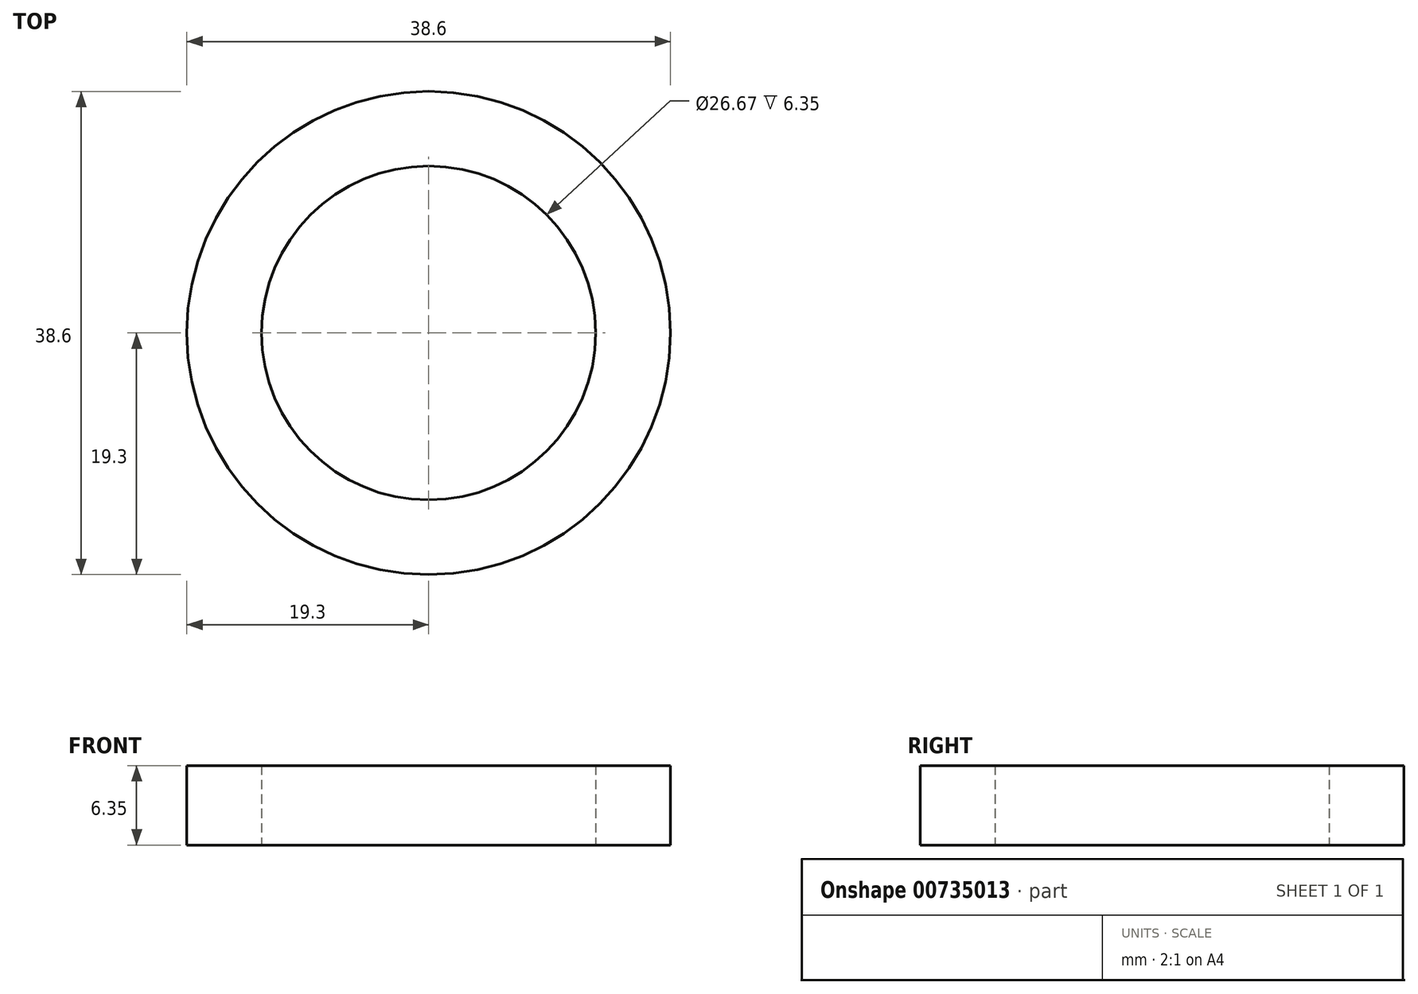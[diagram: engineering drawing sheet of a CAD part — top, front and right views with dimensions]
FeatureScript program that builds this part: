
annotation { "Feature Type Name" : "Feature", "Feature Type Description" : "" }
export const myFeature = defineFeature(function(context is Context, id is Id, definition is map)
    precondition{}
    {
        {
            var Q0;
            Q0=qCreatedBy(makeId("Top.planeOp"),FACE);
            var sketch = newSketch(context, id + "F0", { "sketchPlane" : qUnion([Q0])});
            skCircle(sketch, "E0", {"center": v(0, 0) * mm, "radius": 13.34 * mm});
            skCircle(sketch, "E1", {"center": v(0, 0) * mm, "radius": 19.3 * mm});
            skSolve(sketch);
        }
        {
            var Q0;
            Q0 = qSketchRegion(id + "F0", true);
            extrude(context, id + "F1", {"entities" : qUnion([Q0]), "depth" : 6.35 * mm, "offsetDistance" : 25.4 * mm});
        }
    });
